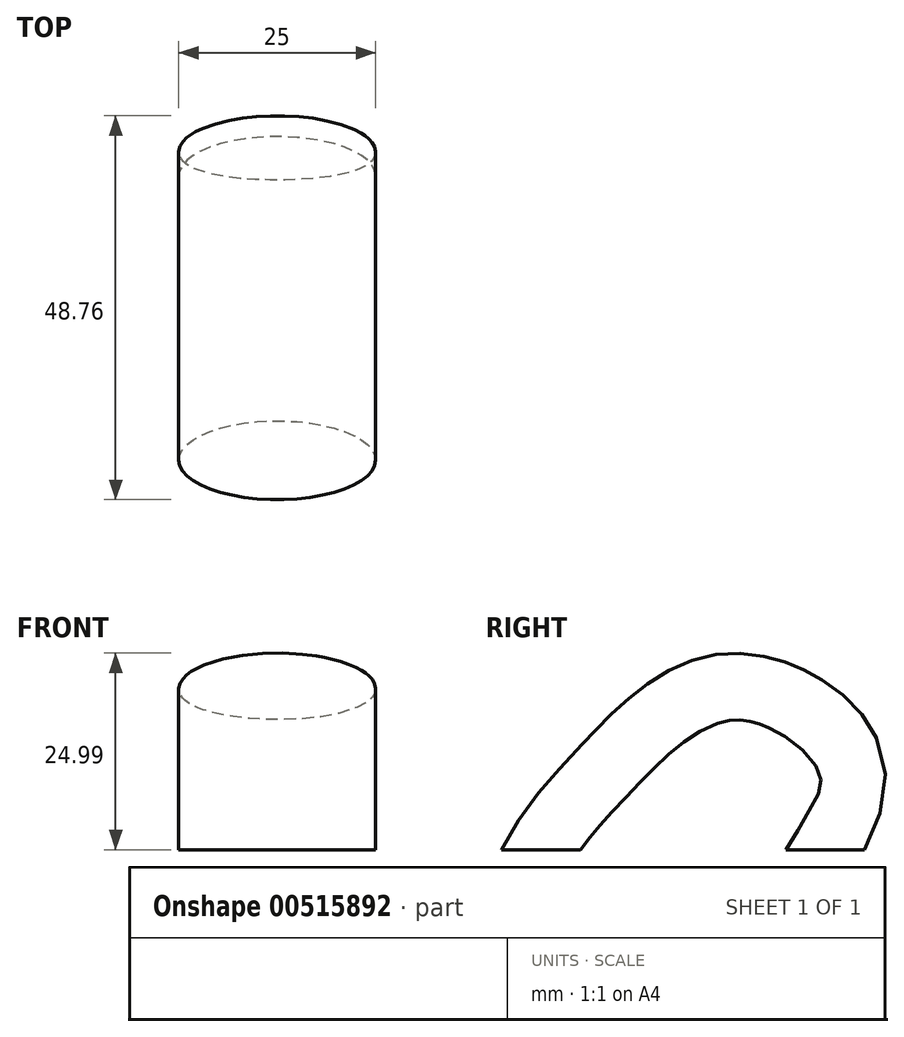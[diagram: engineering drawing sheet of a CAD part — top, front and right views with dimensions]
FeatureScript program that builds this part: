
annotation { "Feature Type Name" : "Feature", "Feature Type Description" : "" }
export const myFeature = defineFeature(function(context is Context, id is Id, definition is map)
    precondition{}
    {
        {
            var Q0;
            Q0=qCreatedBy(makeId("Top.planeOp"),FACE);
            var sketch = newSketch(context, id + "F0", { "sketchPlane" : qUnion([Q0])});
            skEllipse(sketch, "E0", {"center": v(0, 0) * mm, "majorRadius": 12.5 * mm, "minorRadius": 5 * mm, "majorAxis": v(1, 0)});
            skSolve(sketch);
        }
        {
            var Q0;
            Q0=qCreatedBy(makeId("Right.planeOp"),FACE);
            var sketch = newSketch(context, id + "F1", { "sketchPlane" : qUnion([Q0])});
            skFitSpline(sketch, "E1", {"points": [v(0, 0) * mm, v(1.7, 13.53) * mm, v(-12.8, 20.4) * mm, v(-28.37, 9.7) * mm, v(-36.1, 0) * mm], "startDerivative": vector(42.6, 73.8) * mm, "endDerivative": vector(-27.38, -47.43) * mm});
            skLineSegment(sketch, "E2", {"start": v(0, 0) * mm, "end": v(15.13, 0) * mm, "construction": true});
            skLineSegment(sketch, "E3", {"start": v(0, 0) * mm, "end": v(-8.16, -14.13) * mm, "construction": true});
            skLineSegment(sketch, "E4", {"start": v(-36.1, 0) * mm, "end": v(-13.77, 38.7) * mm, "construction": true});
            skSolve(sketch);
        }
        {
            var Q0;
            Q0=makeQuery(id+"F0.imprint","IMPRINT",FACE,{"disambiguationData":[TD([[makeQuery(id+"F0.imprint","IMPRINT",EDGE,{"derivedFrom":sQuery(id+"F0.wireOp",EDGE,"E0")}),1.0]])]});
            var Q1;
            Q1=sQuery(id+"F1.wireOp",EDGE,"E1");
            sweep(context, id + "F2", {"profiles" : qUnion([Q0]), "path" : qUnion([Q1])});
        }
    });
